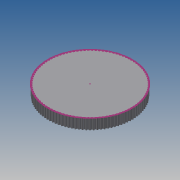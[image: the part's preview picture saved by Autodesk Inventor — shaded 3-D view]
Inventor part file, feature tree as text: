
AUTODESK INVENTOR PART (.ipt)
format: ipt  version: 2013 (Build 170138000, 138)  size: 1,057,280 bytes
history: native  units: mm
features: sketch x2, extrude x1, pattern_circular x1
ambient origin geometry x8: Origin, YZ Plane, XZ Plane, XY Plane, X Axis, Y Axis, Z Axis, Center Point
bodies: Solid1 (feature_tree)
feature tree (4):
  extrude  "Extrusion1"  Depth=0.628319mm
  pattern_circular  "Circular Pattern1"  [2 undecoded]
  sketch  "Sketch2"  dims[d11=0.254mm d12=0.3mm d13=0.4mm d14=1.0mm d15=0.555mm d16=0.75mm d17=0.254mm d18=8.0mm d19=0.0mm d20=1000.0mm d21=360.0deg d23=0.1mm]
  sketch  "Sketch1"  dims[d0=63.661977mm d9=0.628319mm]
note: 2 required parameter values undecoded (feature->parameter linkage not recoverable at this tier; creation-order binding heuristic only, values carry confidence <= 0.55)
